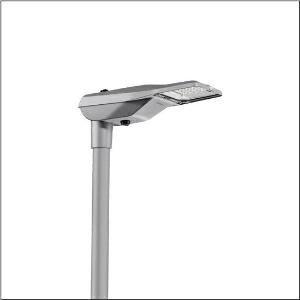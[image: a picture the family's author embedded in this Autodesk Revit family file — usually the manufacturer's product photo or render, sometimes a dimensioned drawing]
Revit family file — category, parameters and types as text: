
# Revit family: streetlight_sl_21_micro___st1_0a_5xe1d33t08db_ddb2
name_source: partatom
category: Lighting Fixtures
units: mm (PartAtom-declared; Revit-internal decimal feet)

## family parameters
Cut with Voids When Loaded = No
Host = Face
Light Source = No
Part Type = Normal
Room Calculation Point = No
Round Connector Dimension = Use Diameter
Shared = No

## types (1)
- --- (1 x LED, 5110 lm, 39.1 W, 3000K)
    Apparent Load = 39 VA
    CIE Flux Codes = 37 72 97 100 100
    Color Rendering = 70
    Color Temperature = 3000K
    Default Elevation = 1800 mm
    Description = Streetlight SL 21 micro, mast luminaire, primary light control with lens, of PMMA, primary optical cover: cover, of toughened safety glass, transparent, light distribution: ST1.0a, light emission: direct distribution, primary light characteristic: asymmetric, installation type: side-entry, post-top, LED, High Power LED, rated luminous flux: 5.110lm, luminous efficacy: 131lm/W, light colour: 730, colour temperature: 3000K, control: flexible luminous flux parameterisation, time-dependent luminous flux control, constant luminous flux control, overheat protection, presetting dimming logarithmic, mains connection: 220..240V, AC, 50/60Hz, start of lifetime: 39W, end of service life: 41W, reduction: 18W, luminaire housing, of diecast aluminium, powder-coated, Siteco® metallic grey (DB 702S), corrosivity category C5 mid according to DIN EN ISO 12944, please order mast flange separately, inclination adjustable: 0°, 5°, 10°, 15°, sealing non-destructively replaceable, multi-level sealing system, length: 528mm, width: 235mm, height: 110mm, mast flange for spigot size: 42mm (side-entry): 5XC10008XM4, 60/48mm (side-entry/post-top): 5XC10108XM2, 76/60mm (side-entry/post-top): 5XC10108XM1, Smart Interface below and above, protection rating (complete): IP66, insulation class (complete): insulation class II (safety insulation), certification: CE, ENEC, ENEC+, VDE, impact resistance: IK09, permissible operating ambient temperature for outdoor applications: -40..+50°C, standard-compliant lighting for roads and squares, packaging unit: 1 piece

Light Distribution: ST1.0a
    Height = 110 mm
    Lamp = 1 x LED
    Lamp Light Flux = 5110 lm
    Lamp Power = 39.1 W
    Lamp count = 1
    Length = 528 mm
    Luminous efficacy = 131 lm/W
    Manufacturer = Siteco
    ModVariant = No
    Model = 5XE1D33T08DB
    Number of Poles = 1
    OnlyDefault = Yes
    Power Factor = 1
    Product Name = Streetlight SL 21 micro | ST1.0a
    Product group = mast luminaire | pylon top
    ProductGroupID = 6100
    Protection Class = Protection class II
    Protection Degree = IP 66
    RLX_Detail_Level = 1
    RLX_Emergency_Light_Flux = 0 lm
    RLX_Emergency_Type = 0
    RLX_Emergency_Type_DB = No
    RlxData = <blob elided: 98693 chars, md5=f125d226>
    Socket = socket
    Standby Power = 0 W
    System Light Flux = 5110 lm
    System Power = 39 W
    Type Comments = factory setting: luminous flux: 100 % | dim-lin: 254 | 765 mA
    Type Image = l_1007239.jpg
    URL = http://relux.com
    VarID = @adj_088063
    Voltage = 0 V
    Weight = 0.00 kg
    Width = 235 mm

## geometry (parser evidence)
native form markers: Blend x4, Sweep x11
no freeform markers — native parametric forms only
